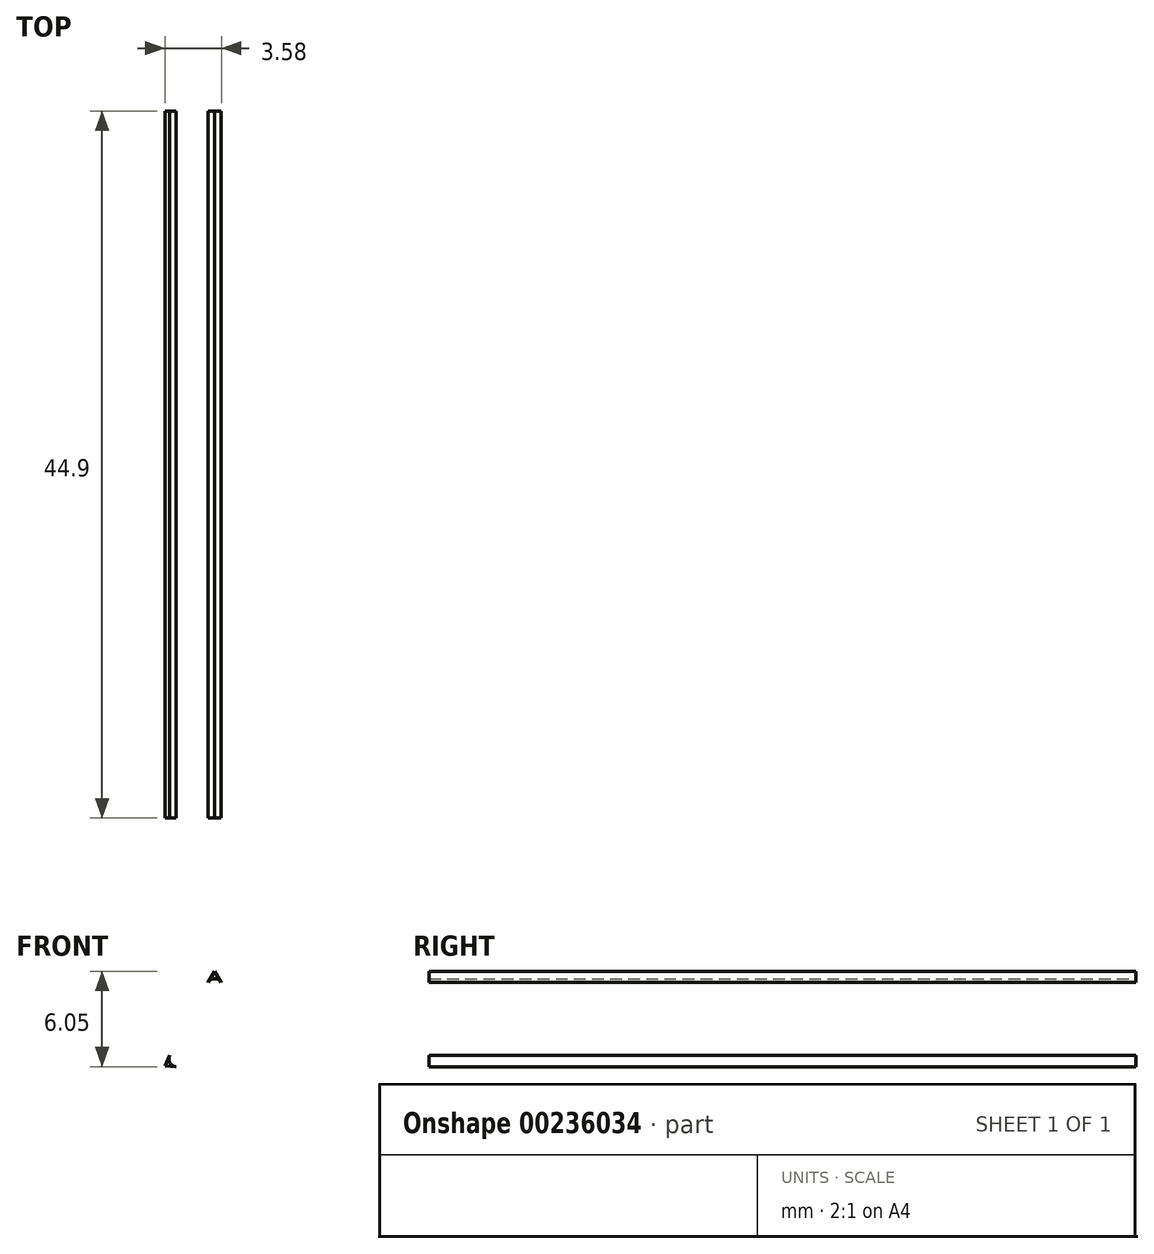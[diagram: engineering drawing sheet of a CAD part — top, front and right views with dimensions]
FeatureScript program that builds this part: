
annotation { "Feature Type Name" : "Feature", "Feature Type Description" : "" }
export const myFeature = defineFeature(function(context is Context, id is Id, definition is map)
    precondition{}
    {
        {
            var Q0;
            Q0=qCreatedBy(makeId("Front.planeOp"),FACE);
            var sketch = newSketch(context, id + "F0", { "sketchPlane" : qUnion([Q0])});
            skFitSpline(sketch, "E0", {"points": [v(0, 0) * mm, v(1.44, 3.07) * mm, v(3.15, 6) * mm], "startDerivative": vector(2.75, 6.2) * mm, "endDerivative": vector(3.55, 5.8) * mm});
            skFitSpline(sketch, "E1", {"points": [v(3.15, 6) * mm, v(4.86, 3.07) * mm, v(6.3, 0) * mm], "startDerivative": vector(3.55, -5.8) * mm, "endDerivative": vector(2.75, -6.2) * mm});
            skFitSpline(sketch, "E2", {"points": [v(6.3, 0) * mm, v(3.15, -0.15) * mm, v(0, 0) * mm], "startDerivative": vector(-6.3, -0.45) * mm, "endDerivative": vector(-6.3, 0.45) * mm});
            skArc(sketch, "E3.filletArc", {"start": v(3.58, 5.3) * mm, "mid": v(3.15, 5.54) * mm, "end": v(2.72, 5.3) * mm});
            skArc(sketch, "E4.filletArc", {"start": v(5.59, -0.05) * mm, "mid": v(5.98, 0.2) * mm, "end": v(6, 0.65) * mm});
            skArc(sketch, "E5.filletArc", {"start": v(0.3, 0.65) * mm, "mid": v(0.32, 0.2) * mm, "end": v(0.71, -0.05) * mm});
            skSolve(sketch);
        }
        {
            var Q0;
            Q0=makeQuery(id+"F0.imprint","IMPRINT",FACE,{"disambiguationData":[TD([[makeQuery(id+"F0.imprint","IMPRINT",EDGE,{"derivedFrom":sQuery(id+"F0.wireOp",EDGE,"E0")}),-1.0]])]});
            extrude(context, id + "F1", {"entities" : qUnion([Q0]), "depth" : 44.9 * mm});
        }
    });
